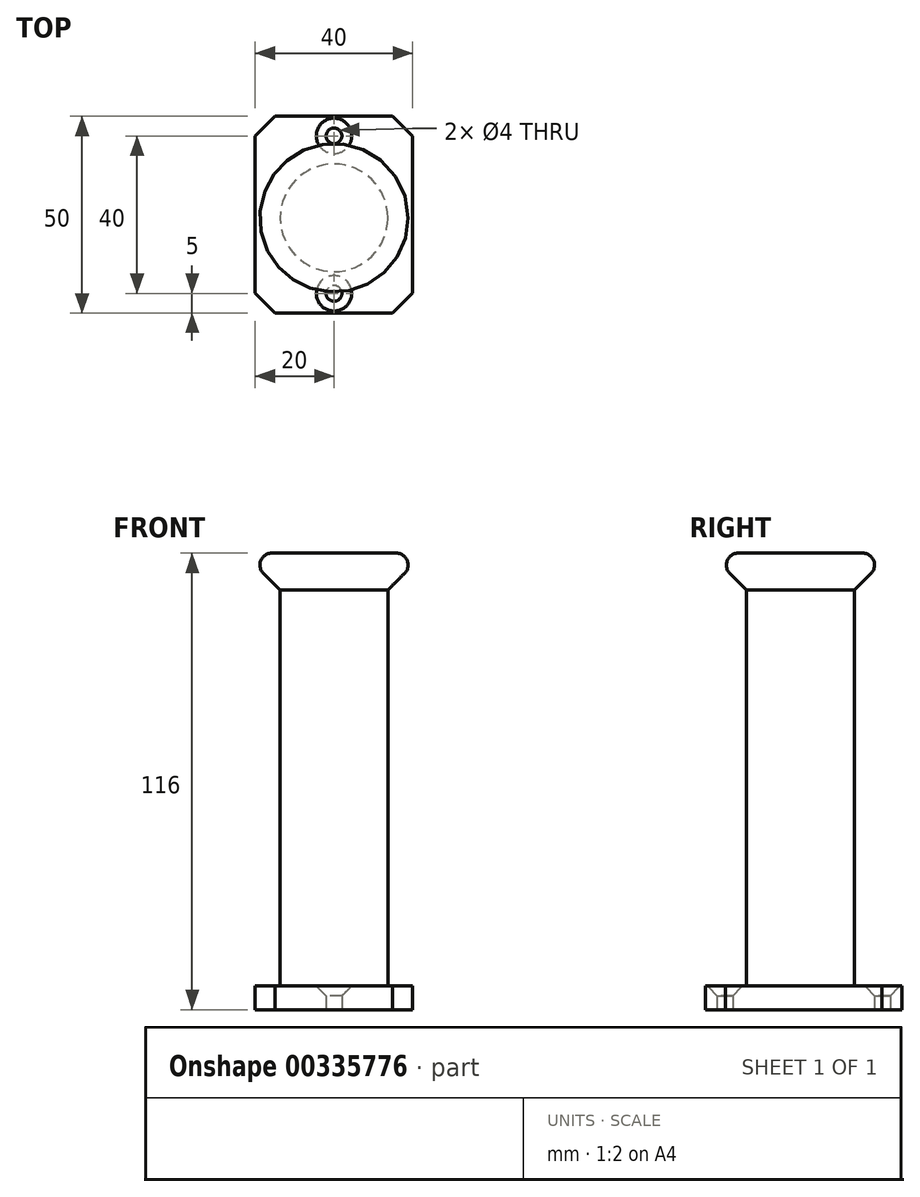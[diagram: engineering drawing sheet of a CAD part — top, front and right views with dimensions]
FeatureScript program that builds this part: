
annotation { "Feature Type Name" : "Feature", "Feature Type Description" : "" }
export const myFeature = defineFeature(function(context is Context, id is Id, definition is map)
    precondition{}
    {
        {
            var Q0;
            Q0=qCreatedBy(makeId("Top.planeOp"),FACE);
            var sketch = newSketch(context, id + "F0", { "sketchPlane" : qUnion([Q0])});
            skLineSegment(sketch, "E0.bottom", {"start": v(0, 0) * mm, "end": v(40, 0) * mm});
            skLineSegment(sketch, "E0.top", {"start": v(0, 50) * mm, "end": v(40, 50) * mm});
            skLineSegment(sketch, "E0.left", {"start": v(0, 0) * mm, "end": v(0, 50) * mm});
            skLineSegment(sketch, "E0.right", {"start": v(40, 0) * mm, "end": v(40, 50) * mm});
            skCircle(sketch, "E1", {"center": v(20, 5) * mm, "radius": 2 * mm});
            skCircle(sketch, "E2", {"center": v(20, 45) * mm, "radius": 2 * mm});
            skSolve(sketch);
        }
        {
            var Q0;
            Q0 = qSketchRegion(id + "F0", true);
            extrude(context, id + "F1", {"entities" : qUnion([Q0]), "depth" : 6 * mm});
        }
        {
            var Q0;
            Q0=makeQuery(id+"F1.opExtrude","CAP_FACE",FACE,{"disambiguationData":[OSD([sQuery(id+"F0.wireOp",EDGE,"E0.bottom"),sQuery(id+"F0.wireOp",EDGE,"E0.top"),sQuery(id+"F0.wireOp",EDGE,"E0.left"),sQuery(id+"F0.wireOp",EDGE,"E0.right"),sQuery(id+"F0.wireOp",EDGE,"E1"),sQuery(id+"F0.wireOp",EDGE,"E2")])],"isStart":false});
            var sketch = newSketch(context, id + "F2", { "sketchPlane" : qUnion([Q0])});
            skCircle(sketch, "E3", {"center": v(20, 24.18) * mm, "radius": 13.68 * mm});
            skSolve(sketch);
        }
        {
            var Q0;
            Q0 = qSketchRegion(id + "F2", true);
            extrude(context, id + "F3", {"entities" : qUnion([Q0]), "operationType" : NewBodyOperationType.ADD, "depth" : 100 * mm});
        }
        {
            var Q0;
            Q0=makeQuery(id+"F3.opExtrude","CAP_FACE",FACE,{"disambiguationData":[OSD([sQuery(id+"F2.wireOp",EDGE,"E3")])],"isStart":false});
            var sketch = newSketch(context, id + "F4", { "sketchPlane" : qUnion([Q0])});
            skCircle(sketch, "E4", {"center": v(20, 24.18) * mm, "radius": 23.06 * mm});
            skSolve(sketch);
        }
        {
            var Q0;
            Q0 = qSketchRegion(id + "F4", true);
            extrude(context, id + "F5", {"entities" : qUnion([Q0]), "operationType" : NewBodyOperationType.ADD, "depth" : 10 * mm});
        }
        {
            var Q0;
            Q0=makeQuery(id+"F5.opExtrude","CAP_EDGE",EDGE,{"disambiguationData":[OSD([sQuery(id+"F4.wireOp",EDGE,"E4")])],"isStart":true});
            chamfer(context, id + "F6", {"entities" : qUnion([Q0]), "width" : 10 * mm, "tangentPropagation" : true});
        }
        {
            var Q0;
            {var subQ0=sQuery(id+"F4.wireOp",EDGE,"E4");Q0=makeQuery(id+"F6.opChamfer","BLEND_EDGE",EDGE,{"blendedFrom":[makeQuery(id+"F5.opExtrude","CAP_EDGE",EDGE,{"disambiguationData":[OSD([subQ0])],"isStart":true}),makeQuery(id+"F5.opExtrude","CAP_FACE",FACE,{"disambiguationData":[OSD([subQ0])],"isStart":false})],"blendedInto":[makeQuery(id+"F5.opExtrude","CAP_FACE",FACE,{"disambiguationData":[OSD([subQ0])],"isStart":false})]});}
            fillet(context, id + "F7", {"entities" : qUnion([Q0]), "radius" : 3 * mm, "tangentPropagation" : true, "allowEdgeOverflow" : false});
        }
        {
            var Q0;
            Q0=makeQuery(id+"F1.opExtrude","SWEPT_EDGE",EDGE,{"disambiguationData":[OSD([sQuery(id+"F0.wireOp",EDGE,"E0.bottom"),sQuery(id+"F0.wireOp",EDGE,"E0.right")])]});
            var Q1;
            Q1=makeQuery(id+"F1.opExtrude","SWEPT_EDGE",EDGE,{"disambiguationData":[OSD([sQuery(id+"F0.wireOp",EDGE,"E0.top"),sQuery(id+"F0.wireOp",EDGE,"E0.right")])]});
            var Q2;
            Q2=makeQuery(id+"F1.opExtrude","SWEPT_EDGE",EDGE,{"disambiguationData":[OSD([sQuery(id+"F0.wireOp",EDGE,"E0.top"),sQuery(id+"F0.wireOp",EDGE,"E0.left")])]});
            var Q3;
            Q3=makeQuery(id+"F1.opExtrude","SWEPT_EDGE",EDGE,{"disambiguationData":[OSD([sQuery(id+"F0.wireOp",EDGE,"E0.bottom"),sQuery(id+"F0.wireOp",EDGE,"E0.left")])]});
            chamfer(context, id + "F8", {"entities" : qUnion([Q0, Q1, Q2, Q3]), "width" : 5.08 * mm, "tangentPropagation" : true});
        }
        {
            var Q0;
            Q0=makeQuery(id+"F1.opExtrude","CAP_EDGE",EDGE,{"disambiguationData":[OSD([sQuery(id+"F0.wireOp",EDGE,"E1")])],"isStart":false});
            var Q1;
            Q1=makeQuery(id+"F1.opExtrude","CAP_EDGE",EDGE,{"disambiguationData":[OSD([sQuery(id+"F0.wireOp",EDGE,"E2")])],"isStart":false});
            chamfer(context, id + "F9", {"entities" : qUnion([Q0, Q1]), "width" : 2.5 * mm, "tangentPropagation" : true});
        }
    });
